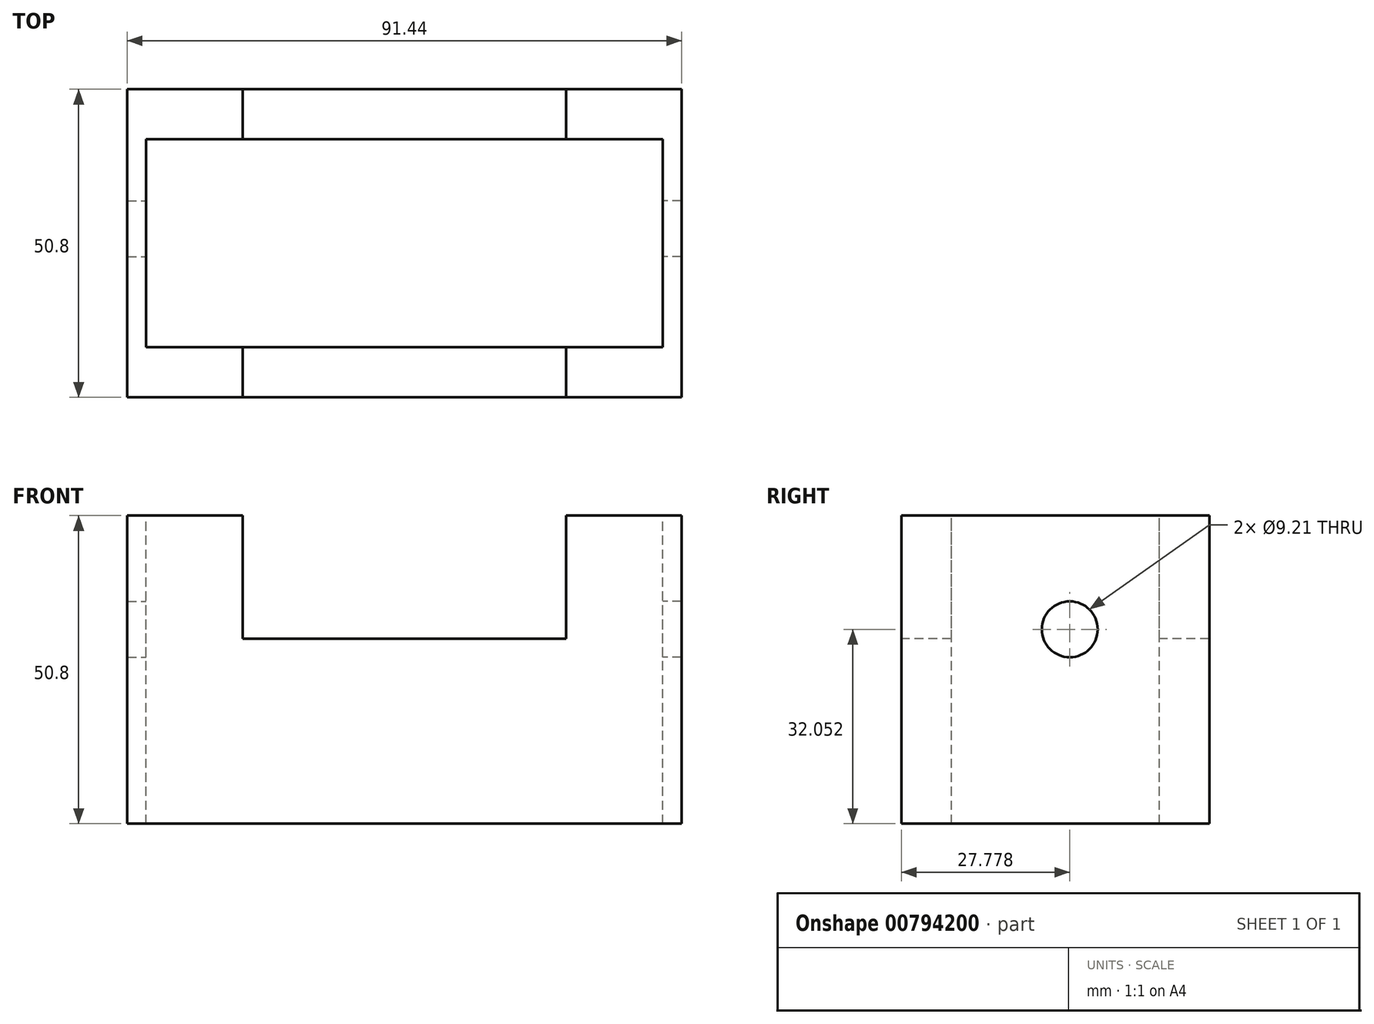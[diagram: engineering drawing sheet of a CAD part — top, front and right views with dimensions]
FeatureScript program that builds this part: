
annotation { "Feature Type Name" : "Feature", "Feature Type Description" : "" }
export const myFeature = defineFeature(function(context is Context, id is Id, definition is map)
    precondition{}
    {
        {
            var Q0;
            Q0=qCreatedBy(makeId("Front.planeOp"),FACE);
            var sketch = newSketch(context, id + "F0", { "sketchPlane" : qUnion([Q0])});
            skLineSegment(sketch, "E0", {"start": v(0, 0) * mm, "end": v(-26.67, 0) * mm});
            skLineSegment(sketch, "E1", {"start": v(-26.67, 0) * mm, "end": v(-26.67, 20.32) * mm});
            skLineSegment(sketch, "E2", {"start": v(0, -30.48) * mm, "end": v(-45.72, -30.48) * mm});
            skLineSegment(sketch, "E3", {"start": v(-45.72, -30.48) * mm, "end": v(-45.72, 20.32) * mm});
            skLineSegment(sketch, "E4", {"start": v(-26.67, 20.32) * mm, "end": v(-45.72, 20.32) * mm});
            skLineSegment(sketch, "E5", {"start": v(0, 0) * mm, "end": v(0, -30.48) * mm});
            skSolve(sketch);
        }
        {
            var Q0;
            Q0=makeQuery(id+"F0.imprint","IMPRINT",FACE,{"disambiguationData":[TD([[makeQuery(id+"F0.imprint","IMPRINT",EDGE,{"derivedFrom":sQuery(id+"F0.wireOp",EDGE,"E0")}),1.0]])]});
            extrude(context, id + "F1", {"entities" : qUnion([Q0]), "oppositeDirection" : true, "depth" : 50.8 * mm, "offsetDistance" : 25.4 * mm});
        }
        {
            var Q0;
            Q0=makeQuery(id+"F1.opExtrude","SWEPT_FACE",FACE,{"disambiguationData":[OSD([sQuery(id+"F0.wireOp",EDGE,"E4")])]});
            var sketch = newSketch(context, id + "F2", { "sketchPlane" : qUnion([Q0])});
            skLineSegment(sketch, "E6", {"start": v(-26.67, 0) * mm, "end": v(-26.67, 8.26) * mm});
            skLineSegment(sketch, "E7", {"start": v(-26.67, 50.8) * mm, "end": v(-26.67, 42.55) * mm});
            skLineSegment(sketch, "E8", {"start": v(-26.67, 8.26) * mm, "end": v(-42.6, 8.26) * mm});
            skLineSegment(sketch, "E9", {"start": v(-26.67, 42.55) * mm, "end": v(-42.6, 42.55) * mm});
            skLineSegment(sketch, "E10", {"start": v(-42.6, 8.26) * mm, "end": v(-42.6, 42.55) * mm});
            skSolve(sketch);
        }
        {
            var Q0;
            Q0=makeQuery(id+"F1.opExtrude","SWEPT_FACE",FACE,{"disambiguationData":[OSD([sQuery(id+"F0.wireOp",EDGE,"E0")])]});
            var sketch = newSketch(context, id + "F3", { "sketchPlane" : qUnion([Q0])});
            skLineSegment(sketch, "E11", {"start": v(0, 0) * mm, "end": v(0, 8.26) * mm});
            skLineSegment(sketch, "E12", {"start": v(0, 50.8) * mm, "end": v(0, 42.55) * mm});
            skLineSegment(sketch, "E13", {"start": v(0, 8.26) * mm, "end": v(-26.67, 8.26) * mm});
            skLineSegment(sketch, "E14", {"start": v(0, 42.55) * mm, "end": v(-26.67, 42.55) * mm});
            skSolve(sketch);
        }
        {
            var Q0;
            {var subQ0=sQuery(id+"F2.wireOp",EDGE,"E8");Q0=makeQuery(id+"F2.imprint","IMPRINT",FACE,{"disambiguationData":[TD([[makeQuery(id+"F2.imprint","IMPRINT",EDGE,{"derivedFrom":subQ0}),-1.0]])]});}
            extrude(context, id + "F4", {"entities" : qUnion([Q0]), "operationType" : NewBodyOperationType.REMOVE, "oppositeDirection" : true, "depth" : 25.4 * mm, "offsetDistance" : 25.4 * mm});
        }
        {
            var Q0;
            {var subQ0=sQuery(id+"F3.wireOp",EDGE,"E13");Q0=makeQuery(id+"F3.imprint","IMPRINT",FACE,{"disambiguationData":[TD([[makeQuery(id+"F3.imprint","IMPRINT",EDGE,{"derivedFrom":subQ0}),-1.0]])]});}
            extrude(context, id + "F5", {"entities" : qUnion([Q0]), "operationType" : NewBodyOperationType.REMOVE, "oppositeDirection" : true, "depth" : 25.4 * mm, "offsetDistance" : 25.4 * mm});
        }
        {
            var Q0;
            Q0=makeQuery(id+"F4.boolean.opBoolean","COPY",FACE,{"derivedFrom":makeQuery(id+"F4.opExtrude","CAP_FACE",FACE,{"disambiguationData":[OSD([sQuery(id+"F0.wireOp",EDGE,"E1"),sQuery(id+"F0.wireOp",EDGE,"E4"),sQuery(id+"F2.wireOp",EDGE,"E8"),sQuery(id+"F2.wireOp",EDGE,"E9"),sQuery(id+"F2.wireOp",EDGE,"E10")])],"isStart":false})});
            extrude(context, id + "F6", {"entities" : qUnion([Q0]), "operationType" : NewBodyOperationType.REMOVE, "oppositeDirection" : true, "depth" : 25.4 * mm, "offsetDistance" : 25.4 * mm});
        }
        {
            var Q0;
            Q0=makeQuery(id+"F1.opExtrude","SWEPT_FACE",FACE,{"disambiguationData":[OSD([sQuery(id+"F0.wireOp",EDGE,"E2")])]});
            var sketch = newSketch(context, id + "F7", { "sketchPlane" : qUnion([Q0])});
            skLineSegment(sketch, "E15.bottom", {"start": v(-26.67, -42.55) * mm, "end": v(-42.6, -42.55) * mm});
            skLineSegment(sketch, "E15.top", {"start": v(-26.67, -8.26) * mm, "end": v(-42.6, -8.26) * mm});
            skLineSegment(sketch, "E15.left", {"start": v(-26.67, -42.55) * mm, "end": v(-26.67, -8.26) * mm});
            skLineSegment(sketch, "E15.right", {"start": v(-42.6, -42.55) * mm, "end": v(-42.6, -8.26) * mm});
            skSolve(sketch);
        }
        {
            var Q0;
            Q0=makeQuery(id+"F7.imprint","IMPRINT",FACE,{"disambiguationData":[TD([[makeQuery(id+"F7.imprint","IMPRINT",EDGE,{"derivedFrom":sQuery(id+"F7.wireOp",EDGE,"E15.bottom")}),-1.0]])]});
            extrude(context, id + "F8", {"entities" : qUnion([Q0]), "operationType" : NewBodyOperationType.ADD, "oppositeDirection" : true, "depth" : 5.08 * mm, "offsetDistance" : 25.4 * mm});
        }
        {
            var Q0;
            {var subQ0=sQuery(id+"F2.wireOp",EDGE,"E10");Q0=makeQuery(id+"F6.boolean.opBoolean","MERGE",FACE,{"derivedFrom":[makeQuery(id+"F4.boolean.opBoolean","COPY",FACE,{"derivedFrom":makeQuery(id+"F4.opExtrude","SWEPT_FACE",FACE,{"disambiguationData":[OSD([subQ0])]})}),makeQuery(id+"F6.opExtrude","SWEPT_FACE",FACE,{"disambiguationData":[OSD([subQ0])]})]});}
            var sketch = newSketch(context, id + "F9", { "sketchPlane" : qUnion([Q0])});
            skCircle(sketch, "E16", {"center": v(27.78, 1.57) * mm, "radius": 4.6 * mm});
            skSolve(sketch);
        }
        {
            var Q0;
            Q0=makeQuery(id+"F9.imprint","IMPRINT",FACE,{"disambiguationData":[TD([[makeQuery(id+"F9.imprint","IMPRINT",EDGE,{"derivedFrom":sQuery(id+"F9.wireOp",EDGE,"E16")}),1.0]])]});
            extrude(context, id + "F10", {"entities" : qUnion([Q0]), "operationType" : NewBodyOperationType.REMOVE, "oppositeDirection" : true, "depth" : 25.4 * mm, "offsetDistance" : 25.4 * mm});
        }
        {
            var Q0;
            Q0=makeQuery(id+"F1.opExtrude","SWEPT_BODY",BODY,{"disambiguationData":[OSD([sQuery(id+"F0.wireOp",EDGE,"E0"),sQuery(id+"F0.wireOp",EDGE,"E1"),sQuery(id+"F0.wireOp",EDGE,"E2"),sQuery(id+"F0.wireOp",EDGE,"E3"),sQuery(id+"F0.wireOp",EDGE,"E4"),sQuery(id+"F0.wireOp",EDGE,"E5")])]});
            var Q1;
            Q1=makeQuery(id+"F1.opExtrude","SWEPT_FACE",FACE,{"disambiguationData":[OSD([sQuery(id+"F0.wireOp",EDGE,"E5")])]});
            mirror(context, id + "F11", {"operationType" : NewBodyOperationType.ADD, "entities" : qUnion([Q0]), "mirrorPlane" : qUnion([Q1])});
        }
        {
            var Q0;
            {var subQ0=makeQuery(id+"F8.boolean.opBoolean","MERGE",FACE,{"derivedFrom":[makeQuery(id+"F5.boolean.opBoolean","COPY",FACE,{"derivedFrom":makeQuery(id+"F5.opExtrude","CAP_FACE",FACE,{"disambiguationData":[OSD([sQuery(id+"F0.wireOp",EDGE,"E0"),sQuery(id+"F0.wireOp",EDGE,"E1"),sQuery(id+"F0.wireOp",EDGE,"E5"),sQuery(id+"F3.wireOp",EDGE,"E13"),sQuery(id+"F3.wireOp",EDGE,"E14")])],"isStart":false})}),makeQuery(id+"F8.opExtrude","CAP_FACE",FACE,{"disambiguationData":[OSD([sQuery(id+"F7.wireOp",EDGE,"E15.bottom"),sQuery(id+"F7.wireOp",EDGE,"E15.top"),sQuery(id+"F7.wireOp",EDGE,"E15.left"),sQuery(id+"F7.wireOp",EDGE,"E15.right")])],"isStart":false})]});Q0=makeQuery(id+"F11.boolean.opBoolean","MERGE",FACE,{"derivedFrom":[subQ0,makeQuery(id+"F11.opPattern","COPY",FACE,{"derivedFrom":subQ0,"instanceName":"1"})]});}
            extrude(context, id + "F12", {"entities" : qUnion([Q0]), "operationType" : NewBodyOperationType.REMOVE, "oppositeDirection" : true, "depth" : 25.4 * mm, "offsetDistance" : 25.4 * mm});
        }
    });
